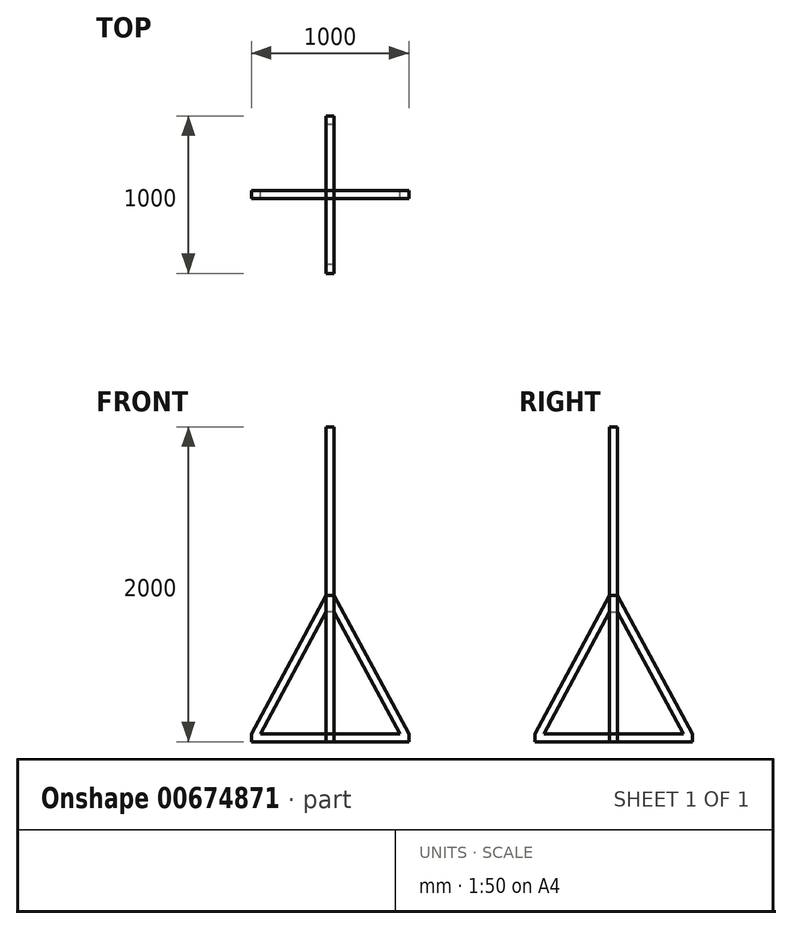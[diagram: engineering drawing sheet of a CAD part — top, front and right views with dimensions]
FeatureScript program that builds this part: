
annotation { "Feature Type Name" : "Feature", "Feature Type Description" : "" }
export const myFeature = defineFeature(function(context is Context, id is Id, definition is map)
    precondition{}
    {
        {
            var Q0;
            Q0=qCreatedBy(makeId("Front.planeOp"),FACE);
            var sketch = newSketch(context, id + "F0", { "sketchPlane" : qUnion([Q0])});
            skLineSegment(sketch, "E0.bottom", {"start": v(0, 0) * mm, "end": v(50, 0) * mm});
            skLineSegment(sketch, "E0.top", {"start": v(0, 1000) * mm, "end": v(50, 1000) * mm});
            skLineSegment(sketch, "E0.left", {"start": v(0, 50) * mm, "end": v(0, 824.72) * mm});
            skLineSegment(sketch, "E0.right", {"start": v(50, 50) * mm, "end": v(50, 824.72) * mm});
            skLineSegment(sketch, "E1.bottom", {"start": v(-475, 0) * mm, "end": v(525, 0) * mm});
            skLineSegment(sketch, "E1.top", {"start": v(-418.18, 50) * mm, "end": v(0, 50) * mm});
            skLineSegment(sketch, "E1.left", {"start": v(-475, 0) * mm, "end": v(-475, 50) * mm});
            skLineSegment(sketch, "E1.right", {"start": v(525, 0) * mm, "end": v(525, 50) * mm});
            skLineSegment(sketch, "E2", {"start": v(-475, 50) * mm, "end": v(0, 929.99) * mm});
            skLineSegment(sketch, "E3", {"start": v(525, 50) * mm, "end": v(50, 929.99) * mm});
            skLineSegment(sketch, "E4", {"start": v(-418.18, 50) * mm, "end": v(0, 824.72) * mm});
            skLineSegment(sketch, "E5", {"start": v(50, 824.72) * mm, "end": v(468.18, 50) * mm});
            skLineSegment(sketch, "E6.trimOffspring", {"start": v(50, 50) * mm, "end": v(468.18, 50) * mm});
            skLineSegment(sketch, "E7.trimOffspring", {"start": v(0, 929.99) * mm, "end": v(0, 1000) * mm});
            skLineSegment(sketch, "E8.trimOffspring", {"start": v(50, 929.99) * mm, "end": v(50, 1000) * mm});
            skSolve(sketch);
        }
        {
            var Q0;
            Q0 = qSketchRegion(id + "F0", true);
            extrude(context, id + "F1", {"entities" : qUnion([Q0]), "endBound" : BoundingType.SYMMETRIC, "depth" : 50 * mm, "offsetDistance" : 25 * mm});
        }
        {
            var Q0;
            Q0=qCreatedBy(makeId("Right.planeOp"),FACE);
            var sketch = newSketch(context, id + "F2", { "sketchPlane" : qUnion([Q0])});
            skLineSegment(sketch, "E9.bottom", {"start": v(-500, 0) * mm, "end": v(500, 0) * mm});
            skLineSegment(sketch, "E9.top", {"start": v(-443.18, 50) * mm, "end": v(-25, 50) * mm});
            skLineSegment(sketch, "E9.left", {"start": v(-500, 0) * mm, "end": v(-500, 50) * mm});
            skLineSegment(sketch, "E9.right", {"start": v(500, 0) * mm, "end": v(500, 50) * mm});
            skLineSegment(sketch, "E10.0", {"start": v(-25, 929.99) * mm, "end": v(25, 929.99) * mm});
            skLineSegment(sketch, "E11", {"start": v(-500, 50) * mm, "end": v(-25, 929.99) * mm});
            skLineSegment(sketch, "E12", {"start": v(500, 50) * mm, "end": v(25, 929.99) * mm});
            skPoint(sketch, "E13.0", {"position": v(-25, 824.72) * mm});
            skPoint(sketch, "E14.0", {"position": v(25, 824.72) * mm});
            skLineSegment(sketch, "E15", {"start": v(-25, 824.72) * mm, "end": v(-443.18, 50) * mm});
            skLineSegment(sketch, "E16", {"start": v(25, 824.72) * mm, "end": v(443.18, 50) * mm});
            skLineSegment(sketch, "E17", {"start": v(-25, 824.72) * mm, "end": v(-25, 50) * mm});
            skPoint(sketch, "E17.endSnap0", {"position": v(0, 50) * mm});
            skLineSegment(sketch, "E18", {"start": v(25, 824.72) * mm, "end": v(25, 50) * mm});
            skLineSegment(sketch, "E19.trimOffspring", {"start": v(25, 50) * mm, "end": v(443.18, 50) * mm});
            skSolve(sketch);
        }
        {
            var Q0;
            Q0=makeQuery(id+"F2.imprint","IMPRINT",FACE,{"disambiguationData":[TD([[makeQuery(id+"F2.imprint","IMPRINT",EDGE,{"derivedFrom":sQuery(id+"F2.wireOp",EDGE,"E9.bottom")}),1.0]])]});
            extrude(context, id + "F3", {"entities" : qUnion([Q0]), "operationType" : NewBodyOperationType.ADD, "depth" : 50 * mm, "offsetDistance" : 25 * mm});
        }
        {
            var Q0;
            Q0=makeQuery(id+"F1.opExtrude","SWEPT_FACE",FACE,{"disambiguationData":[OSD([sQuery(id+"F0.wireOp",EDGE,"E0.top")])]});
            extrude(context, id + "F4", {"entities" : qUnion([Q0]), "operationType" : NewBodyOperationType.ADD, "depth" : 1000 * mm, "offsetDistance" : 25 * mm});
        }
    });
